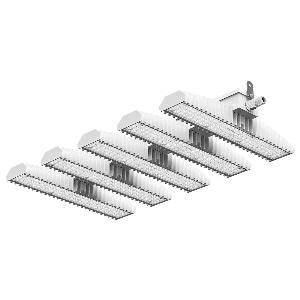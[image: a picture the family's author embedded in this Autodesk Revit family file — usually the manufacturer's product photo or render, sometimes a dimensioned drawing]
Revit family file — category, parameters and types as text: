
# Revit family: 3f_filippi_-_3f_lem_ht_ampio_3f_filippi_-_59030_-_3f_lem_5_ht_led_150_cr_ampio
name_source: partatom
category: Lighting Fixtures
units: mm (PartAtom-declared; Revit-internal decimal feet)

## family parameters
Cut with Voids When Loaded = No
Host = Face
Light Source = No
Part Type = Normal
Room Calculation Point = No
Round Connector Dimension = Use Diameter
Shared = No

## types (1)
- 3F Filippi - 3F LEM HT Ampio (1 x LED, 27174 lm, 170 W, 4000 K)
    Apparent Load = 170 VA
    Approval mark = ENEC
    CIE Flux Codes = 60 92 99 100 100
    Color Rendering = 80
    Color Temperature = 4000 K
    Control Gear = Electronic ballast
    Default Elevation = 1800 mm
    Description = Industrial luminaire with high light output and high luminous efficiency designed with the most innovative technologies for environments with temperature up to 70°C.

ILLUMINOTECHNICAL
Luminous efficiency 100% (DLOR 100%, ULOR 0%).
Initial luminous flux of the luminaire 27174 lm.
Direct symmetric wide distribution: the illuminated area has a rectangular shape.
Installation Interdistance Transv.D = 1.58 x hu - Long.D = 1.45 x hu.
Tabular UGR (CIE 117 - 4H-8H; S=0.25H; 70/50/20): RUG 21.6 - 22.6.
Beam angle: 93° - 99°.
Luminous efficacy 160 lm/W.
Lifetime (L93/B10): 30000 h. (tq+25°C)
Lifetime (L90/B10): 50000 h. (tq+25°C)
Lifetime (L85/B10): 80000 h. (tq+25°C)
Lifetime (L80/B10): 100000 h. (tq+25°C)
Lifetime (L85/B10): 50000 h. (tq+70°C)
Sudden decreased luminous flux after 50000 hours: 0% (C0).
Photobiological safety in compliance with IEC/TR 62778: RG0 risk exempt, (IEC 62471).
In compliance with IEC/EN 62722-2-1 - IEC/EN 62717 standards.
Luminous flux at +70°C: -13.5%.

SOURCE
5 Mid-Power linear LED modules 30W/840.
Energy efficiency class (UE 2019/2020 - UE 2019/2015): C.
CIE 13.3 Colour rendering index: CRI >80 (R9 <50%).
IES TM-30 Fidelity Index: Rf = 84 Rg = 95.
CCT nominal colour temperature 4000 K.
Colour initial tolerance (MacAdam): SDCM 3.

MECHANICAL
Passive modular heatsinks in die-casted aluminium, painted in white colour.
To optimize the thermal management of the LED module, the heatsinks are oversized and provided with self-cleaning of cooling fins.
Wiring body in aluminium and galvanised steel anchored solidly to the sinks and thermally separated.
3F Lens lenses with high luminous efficiency, transparent polycarbonate, fixed to the LED modules.
Fixing brackets in stainless steel.
Luminaire with limited surface temperature. - D - (EN 60598-2-24)
Dimensions: 952x542 mm, height 129 mm. Weight 21.355 kg.
IP65 protection degree.
Mechanical strength to impacts IK08 (5 joule).
Glow-wire test resistance 850°C.

ELECTRICAL
Halogen Free electronic wiring 230V-50/60Hz, power factor 0.95, THD <25%, constant output current, class I, 2 driver.
Power of the luminaire 170 W.
CE - IEC 60598-1 - EN 60598-1.
SAFE FLICKER: PstLM=<1 and SVM=<0.4 (IEC TR 61547-1 and IEC TR 63158), to ensure a more comfortable and safe light.
Luminaire compliant with EN 60598-2-22 for power supply from a centralised emergency system CPSS (Central Power Supply System), not incorporated in the luminaire - high risk areas excluded. The default power and flux are 100% in AC and 100% in DC.
Ambient temperature from -30°C to +70°C.
Temperature class T6 max 85°C.
Quick connection via M20 3P connector with 9-13 mm tightening range.
Power unit positioned on a separate compartment by the LED module to ensure optimum temperatures of cabling components, to be inspectable and maintainable.
Relative humidity UR: <85%.

INSTALLATION
Ceiling / Suspended / Wall.
All accessories dedicated to this product are available on the Catalog and on our website www.3F-Filippi.com.

APPLICATIONS
In commercial environments, exhibition and industrial areas, stores, open areas.
Applications with high ambient temperature up to 70°C.

WARNING
Fixture not suitable for cold stores with an ambient temperature <0°C and/or relative humidity >85%.
Luminaire designed for disposal/recycling at end-of-life.
Replaceable (LED only) light source by a professional. Replaceable control gear by a professional.
    Height = 129 mm
    Lamp = 1 x LED
    Lamp Light Flux = 27174 lm
    Lamp Power = 170 W
    Lamp count = 1
    Length = 952 mm
    Lifetime = 50000 h
    Luminous efficacy = 160 lm/W
    Manufacturer = 3F Filippi
    ModVariant = No
    Model = 3F Filippi - 59030 - 3F LEM 5 HT LED 150 CR AMPIO
    Mounting Place = Ceiling
    Mounting Type = Pendant
    Number of Poles = 1
    OnlyDefault = Yes
    Power Factor = 1
    Product Name = 3F Filippi - 3F LEM HT Ampio
    Product group = pendant luminaire
    ProductGroupID = 9
    Protection Class = Protection class I
    Protection Degree = IP 65
    RLX_Detail_Level = 1
    RLX_Emergency_Light_Flux = 0 lm
    RLX_Emergency_Type = 0
    RLX_Emergency_Type_DB = No
    RlxData = <blob elided: 131573 chars, md5=b5efc576>
    Socket = socket
    Standby Power = 0 W
    System Light Flux = 27174 lm
    System Power = 170 W
    Type Comments = Product without accessories
    Type Image = 3f_filippi_-_lem_5.jpg
    URL = http://relux.com
    VarID = ---
    Voltage = 0 V
    Weight = 0.00 kg
    Width = 542 mm

## geometry (parser evidence)
native form markers: Blend x4, Sweep x14
no freeform markers — native parametric forms only
